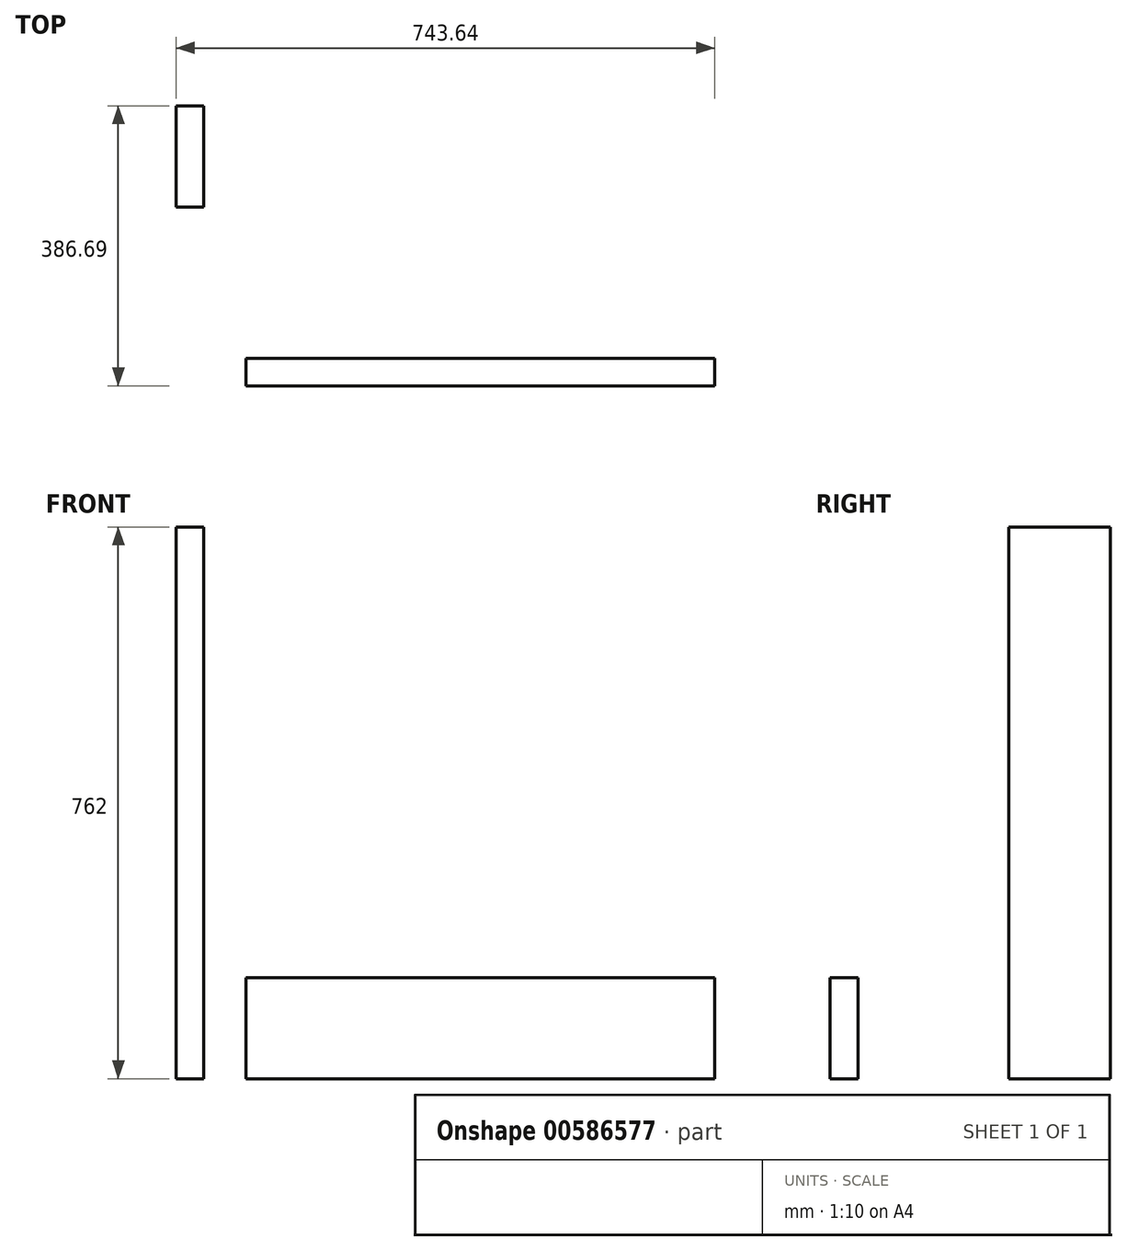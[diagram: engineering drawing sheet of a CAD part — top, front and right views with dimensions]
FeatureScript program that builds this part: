
annotation { "Feature Type Name" : "Feature", "Feature Type Description" : "" }
export const myFeature = defineFeature(function(context is Context, id is Id, definition is map)
    precondition{}
    {
        {
            var Q0;
            Q0=qCreatedBy(makeId("Top.planeOp"),FACE);
            var sketch = newSketch(context, id + "F0", { "sketchPlane" : qUnion([Q0])});
            skLineSegment(sketch, "E0.bottom", {"start": v(-2732.77, -1438.52) * mm, "end": v(-2085.07, -1438.52) * mm});
            skLineSegment(sketch, "E0.top", {"start": v(-2732.77, -1476.62) * mm, "end": v(-2085.07, -1476.62) * mm});
            skLineSegment(sketch, "E0.left", {"start": v(-2732.77, -1438.52) * mm, "end": v(-2732.77, -1476.62) * mm});
            skLineSegment(sketch, "E0.right", {"start": v(-2085.07, -1438.52) * mm, "end": v(-2085.07, -1476.62) * mm});
            skSolve(sketch);
        }
        {
            var Q0;
            Q0 = qSketchRegion(id + "F0", true);
            extrude(context, id + "F1", {"entities" : qUnion([Q0]), "depth" : 139.7 * mm, "offsetDistance" : 25.4 * mm});
        }
        {
            var Q0;
            Q0=qCreatedBy(makeId("Top.planeOp"),FACE);
            var sketch = newSketch(context, id + "F2", { "sketchPlane" : qUnion([Q0])});
            skLineSegment(sketch, "E1.bottom", {"start": v(-2790.61, -1229.63) * mm, "end": v(-2828.71, -1229.63) * mm});
            skLineSegment(sketch, "E1.top", {"start": v(-2790.61, -1089.93) * mm, "end": v(-2828.71, -1089.93) * mm});
            skLineSegment(sketch, "E1.left", {"start": v(-2790.61, -1229.63) * mm, "end": v(-2790.61, -1089.93) * mm});
            skLineSegment(sketch, "E1.right", {"start": v(-2828.71, -1229.63) * mm, "end": v(-2828.71, -1089.93) * mm});
            skSolve(sketch);
        }
        {
            var Q0;
            Q0 = qSketchRegion(id + "F2", true);
            extrude(context, id + "F3", {"entities" : qUnion([Q0]), "depth" : 762 * mm, "offsetDistance" : 25.4 * mm});
        }
    });
